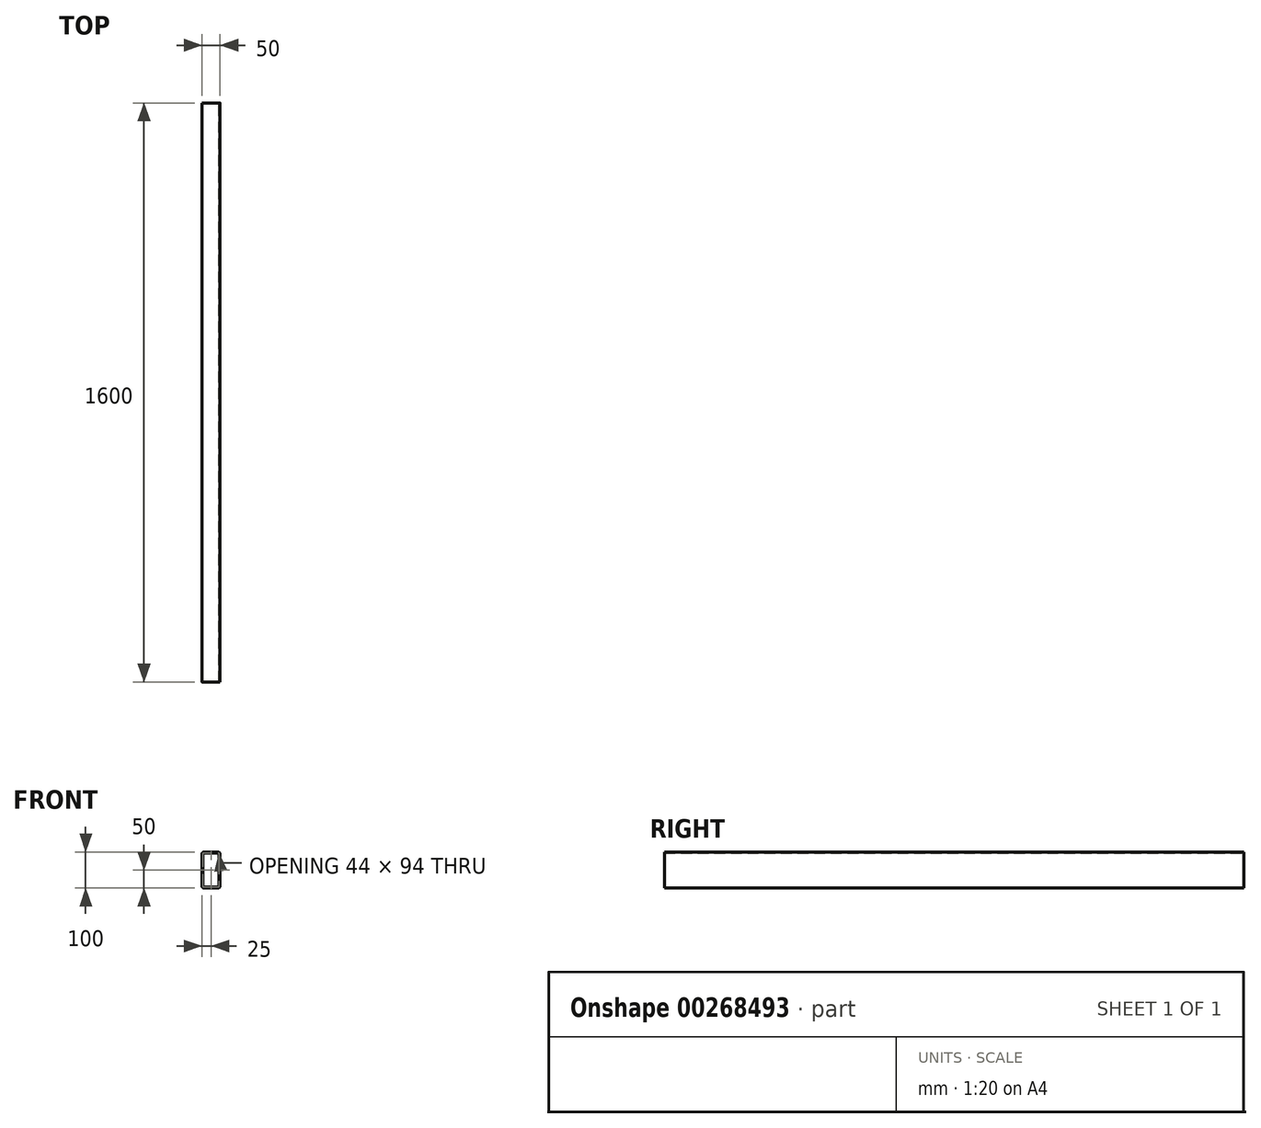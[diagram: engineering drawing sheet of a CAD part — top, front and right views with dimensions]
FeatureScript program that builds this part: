
annotation { "Feature Type Name" : "Feature", "Feature Type Description" : "" }
export const myFeature = defineFeature(function(context is Context, id is Id, definition is map)
    precondition{}
    {
        {
            var Q0;
            Q0=qCreatedBy(makeId("Front.planeOp"),FACE);
            var sketch = newSketch(context, id + "F0", { "sketchPlane" : qUnion([Q0])});
            skLineSegment(sketch, "E0", {"start": v(0, 47) * mm, "end": v(-19, 47) * mm});
            skLineSegment(sketch, "E1", {"start": v(-22, 44) * mm, "end": v(-22, -44) * mm});
            skLineSegment(sketch, "E2", {"start": v(-19, -47) * mm, "end": v(0, -47) * mm});
            skLineSegment(sketch, "E3", {"start": v(0, 50) * mm, "end": v(-19, 50) * mm});
            skLineSegment(sketch, "E4", {"start": v(-25, 44) * mm, "end": v(-25, -44) * mm});
            skLineSegment(sketch, "E5", {"start": v(-19, -50) * mm, "end": v(0, -50) * mm});
            skPoint(sketch, "E6.visualSharp", {"position": v(-22, 47) * mm});
            skArc(sketch, "E6.filletArc", {"start": v(-19, 47) * mm, "mid": v(-21.12, 46.12) * mm, "end": v(-22, 44) * mm});
            skPoint(sketch, "E7.visualSharp", {"position": v(-22, -47) * mm});
            skArc(sketch, "E7.filletArc", {"start": v(-22, -44) * mm, "mid": v(-21.12, -46.12) * mm, "end": v(-19, -47) * mm});
            skPoint(sketch, "E8.visualSharp", {"position": v(-25, 50) * mm});
            skArc(sketch, "E8.filletArc", {"start": v(-19, 50) * mm, "mid": v(-23.24, 48.24) * mm, "end": v(-25, 44) * mm});
            skPoint(sketch, "E9.visualSharp", {"position": v(-25, -50) * mm});
            skArc(sketch, "E9.filletArc", {"start": v(-25, -44) * mm, "mid": v(-23.24, -48.24) * mm, "end": v(-19, -50) * mm});
            skArc(sketch, "E10.MirrorCS", {"start": v(19, 47) * mm, "mid": v(21.12, 46.12) * mm, "end": v(22, 44) * mm});
            skArc(sketch, "E11.MirrorCS", {"start": v(22, -44) * mm, "mid": v(21.12, -46.12) * mm, "end": v(19, -47) * mm});
            skArc(sketch, "E12.MirrorCS", {"start": v(19, 50) * mm, "mid": v(23.24, 48.24) * mm, "end": v(25, 44) * mm});
            skArc(sketch, "E13.MirrorCS", {"start": v(25, -44) * mm, "mid": v(23.24, -48.24) * mm, "end": v(19, -50) * mm});
            skPoint(sketch, "E14.MirrorP", {"position": v(25, 50) * mm});
            skPoint(sketch, "E15.MirrorP", {"position": v(25, -50) * mm});
            skLineSegment(sketch, "E16.MirrorCS", {"start": v(0, 47) * mm, "end": v(19, 47) * mm});
            skPoint(sketch, "E17.MirrorP", {"position": v(22, -47) * mm});
            skLineSegment(sketch, "E18.MirrorCS", {"start": v(22, 44) * mm, "end": v(22, -44) * mm});
            skLineSegment(sketch, "E19.MirrorCS", {"start": v(19, -47) * mm, "end": v(0, -47) * mm});
            skPoint(sketch, "E20.MirrorP", {"position": v(22, 47) * mm});
            skLineSegment(sketch, "E21.MirrorCS", {"start": v(19, -50) * mm, "end": v(0, -50) * mm});
            skLineSegment(sketch, "E22.MirrorCS", {"start": v(0, 50) * mm, "end": v(19, 50) * mm});
            skLineSegment(sketch, "E23.MirrorCS", {"start": v(25, 44) * mm, "end": v(25, -44) * mm});
            skSolve(sketch);
        }
        {
            var Q0;
            Q0=qSketchRegion(id+"F0",true);
            extrude(context, id + "F1", {"entities" : qUnion([Q0]), "depth" : 1600 * mm});
        }
    });
